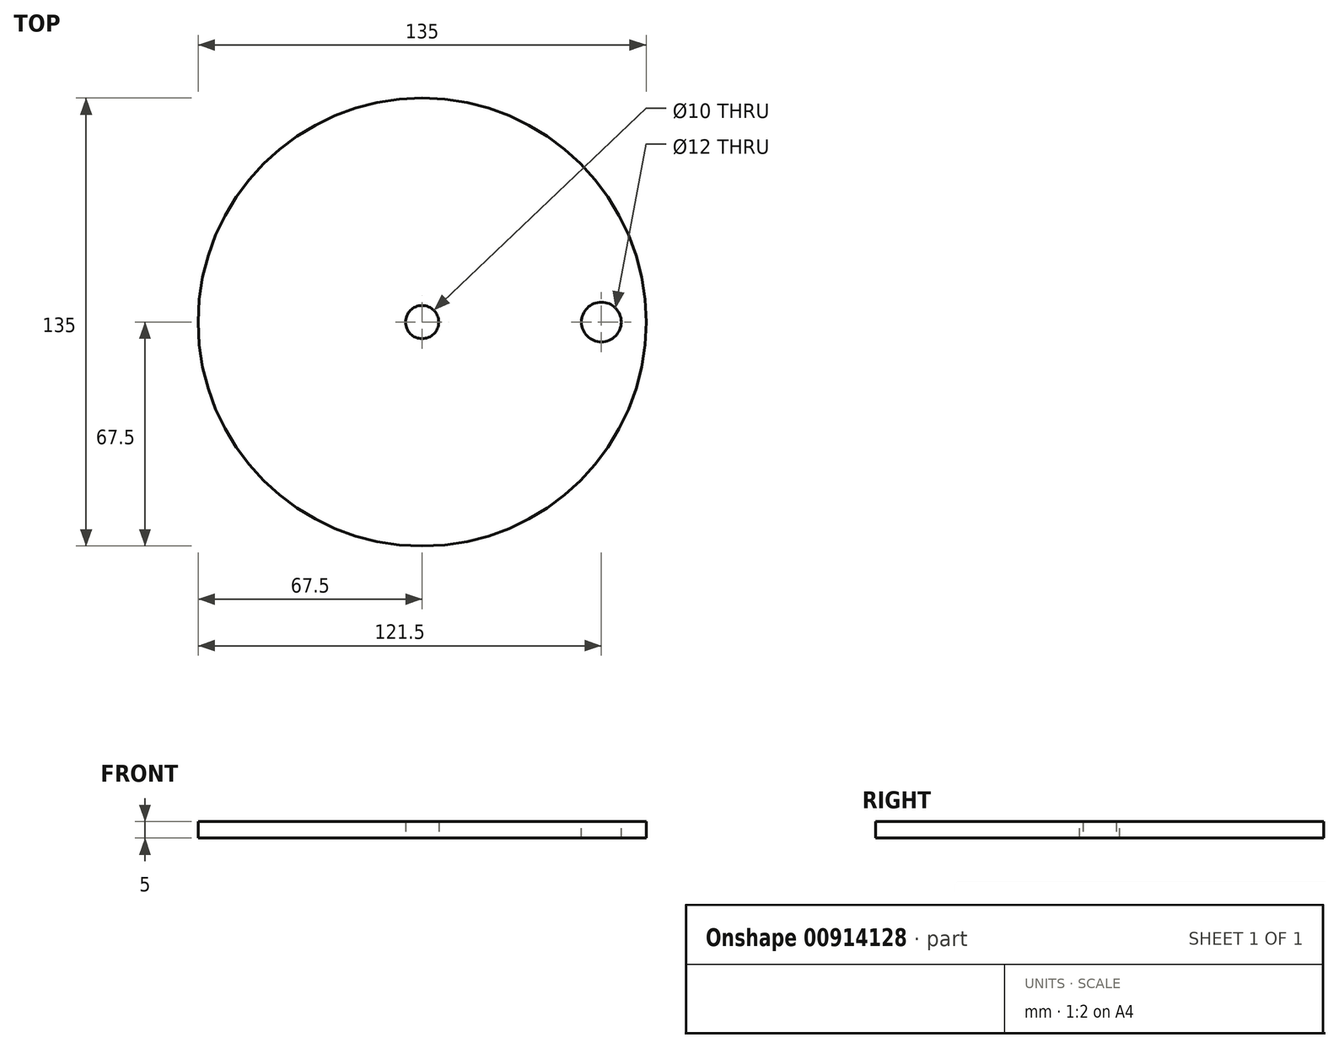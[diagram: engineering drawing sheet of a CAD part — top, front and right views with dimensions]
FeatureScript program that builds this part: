
annotation { "Feature Type Name" : "Feature", "Feature Type Description" : "" }
export const myFeature = defineFeature(function(context is Context, id is Id, definition is map)
    precondition{}
    {
        {
            var Q0;
            Q0=qCreatedBy(makeId("Top.planeOp"),FACE);
            var sketch = newSketch(context, id + "F0", { "sketchPlane" : qUnion([Q0])});
            skPoint(sketch, "E0.middle", {"position": v(0, 0) * mm});
            skCircle(sketch, "E1", {"center": v(0, 0) * mm, "radius": 67.5 * mm});
            skCircle(sketch, "E2", {"center": v(0, 0) * mm, "radius": 5 * mm});
            skSolve(sketch);
        }
        {
            var Q0;
            Q0 = qSketchRegion(id + "F0", true);
            extrude(context, id + "F1", {"entities" : qUnion([Q0]), "depth" : 5 * mm, "offsetDistance" : 25 * mm});
        }
        {
            var Q0;
            Q0=makeQuery(id+"F1.opExtrude","CAP_FACE",FACE,{"disambiguationData":[OSD([sQuery(id+"F0.wireOp",EDGE,"E1"),sQuery(id+"F0.wireOp",EDGE,"E2")])],"isStart":false});
            var sketch = newSketch(context, id + "F2", { "sketchPlane" : qUnion([Q0])});
            skPoint(sketch, "E3", {"position": v(54, 0) * mm});
            skSolve(sketch);
        }
        {
            var Q0;
            Q0=sQuery(id+"F2.wireOp",VERTEX,"E3");
            var Q1;
            Q1=makeQuery(id+"F1.opExtrude","SWEPT_BODY",BODY,{"disambiguationData":[OSD([sQuery(id+"F0.wireOp",EDGE,"E1"),sQuery(id+"F0.wireOp",EDGE,"E2")])]});
            hole(context, id + "F3", {"style" : HoleStyle.SIMPLE, "endStyle" : HoleEndStyle.THROUGH, "standardTappedOrClearance" : lookupTablePath({ "standard" : "ISO", "size" : "12", "type" : "Drilled" }), "standardBlindInLast" : lookupTablePath({ "standard" : "ISO", "size" : "12", "type" : "Drilled" }), "holeDiameter" : 12 * mm, "majorDiameter" : 5 * mm, "isTappedThrough" : true, "tappedDepth" : 14 * mm, "tapClearance" : 3, "locations" : qUnion([Q0]), "scope" : qUnion([Q1])});
        }
    });
